# Revit family: Maxlogic Блок-шлюз GCU
name_source: partatom
category: Fire Alarm Devices
units: mm (PartAtom-declared; Revit-internal decimal feet)

## family parameters
Cut with Voids When Loaded = No
Host = Face
Maintain Annotation Orientation = Yes
OmniClass Number = 23.85.30.21
OmniClass Title = Environmental Detection/Registration
Part Type = Normal
Room Calculation Point = No
Round Connector Dimension = Use Diameter
Shared = No

## types (7) — shared parameters
Manufacturer = Mavili Elektronik Ticaret A.Ş.
Model = Maxlogic
URL = https://www.mavili.com.tr
Адрес №1 = Şerifali Mahallesi Kutup Sokak No:27/1-2-4 Ümraniye TR-34775 İSTANBUL
Вес = 6,200 кг
Вторичный материал = Белый пластмассовый ABS
Гарантийный срок = Года
Гарантийный срок запчастей = 2
Гарантия срока службы = 2
Главный Материал = Серый металлический
Инструкция по установке = https://mavilielektronik.com
Монтажная поверхность = Настенная
Номер телефона = (+)90 216 466 45 05
Номер факса = (+)90 216 466 45 10
Номинальная высота = 300 мм
Номинальная глубина = 100 мм
Номинальная ширина = 400 мм
Рабочая Температура = (-5°C) - (+50°C)
Резервное питание = 220 В Перем. ток
Цвет = Белый
zero-valued in all types: Cost, Default Elevation

## per-type parameters (varying)
| type | Аккумулятор | Код продукта | Производительность кода |
| Система Maxlogic блок-шлюз GCU, вкл. Источник питания 3A и модуль связи TCP / IP | 2 X (12V DC 7 Ah ) | ML-1207.C | EN 54-4 / EN 54-18 |
| Система Maxlogic блок-шлюз GCU, вкл. Источник питания 3A и модуль связи GPRS | 2 X (12V DC 7 Ah ) | ML-1207.G | EN 54-4 / EN 54-18 |
| Система Maxlogic блок-шлюз GCU, вкл. Источник питания 3A и модуль связи RS-232 / RS-485 | 2 X  (12В Пост. ток 7 Aм/ч. ) | ML-1207.K | EN 54-4 / EN 54-18 |
| Система Maxlogic блок-шлюз GCU, вкл. Источник питания 3A и модуль связи Modbus | 2 X  (12В Пост. ток 7 Aм/ч. ) | ML-1207.MX | EN 54-4 / EN 54-18 |
| Система Maxlogic блок-шлюз GCU, вкл. Источник питания 3A и модули связи TCP / IP, GPRS и RS-232 / RS-485 | 2 X  (12В Пост. ток 7 Aм/ч. ) | ML-1207.CGK | EN 54-4 / EN 54-18 |
| Система Maxlogic блок-шлюз GCU, вкл. Источник питания 3A и модуль связи BACnet | 2 X  (12В Пост. ток 7 Aм/ч. ) | ML-1207.B | EN 54-4 / EN 54-18 |
| Система Maxlogic блок-шлюз GCU, вкл. Источник питания 3A и модуль связи NTP Server | 2 х (12В Пост. ток 7 Aм/ч. ) | ML-1207.NTP |  |

note: column(s) folded — value = type name in every type: Description

## geometry (parser evidence)
native form markers: Sweep x2
no freeform markers — native parametric forms only
